# Revit family: 13.3QBR,QBR-M_231217_1
name_source: partatom
category: 통신 장치
units: mm (PartAtom-declared; Revit-internal decimal feet)

## family parameters
OmniClass 번호 = 23.85.10.14.24
OmniClass 제목 = Video Monitors
공유 = 아니오
로드될 때 보이드를 사용하여 절단 = 아니오
룸 계산 점 = 아니오
부품 유형 = 보통
원형 커넥터 치수 = 지름 사용
작업 기준면 기반 = 아니오
주석 방향을 유지합니다. = 아니오
항상 수직 = 예

## types (2) — shared parameters
Active Display Area = 293.76 (H) x 165.24 (V)
Bezel Width (mm) = 12.2  [stored 0.0400262 ft]
Color Gamut = 45%
Contrast Ratio (Typ.) = 800:1
Diagonal Size (Class) = 13
Diagonal Size (Measured) = 13.27
Dimension Package (mm) = 376 x 132 x 248
Dimension Set (mm) = 322.0 x 193.5 x 28.2
Dimension Set Depth (mm) = 28.2
Dimension Set Height (mm) = 193.5  [stored 0.634843 ft]
Dimension Set Width (mm) = 322  [stored 1.05643 ft]
Display Colors = 16.7 M (real 6bit, dither 8bit)
Dynamic C/R = MEGA
EMC = Class B
Environment = ENERGY STAR 8.0, EPEAT
External Control = RS232C(in/out) thru stereo jack, RJ45
H-Scanning Frequency = 30 ~ 81kHZ
Haze = 10%
Input HDCP = HDCP 2.2
Input RGB = -
Input USB = USB 2.0 x 1
Input Video = HDMI 1.4 (1)
Internal Clock Speed = 1.7GHz
Internal Graphics = Graphic resolution : 1920x1080, Output resolution : 1920x1080 (Scale up from graphic processing result.)
Internal IO Ports = USB 2.0
Internal Main Memory Interface = 2.5GB, LPDDR4 1.5GHz 64bit
Internal Multimedia = Video Decoder  : MPEG-1/2/4, H.263, H.264/AVC, UHD H.264/AVC,  VC-1, HEVC, JPEG, PNG, VP8, VP9  *Audio Decoder : AC3 (DD), MPEG
Internal On-Chip Cache Memory = L1 Instruction Cache : 48KB, L1 Data Cache : 32KB, L2 Cache : 2MB
Internal Operating System = Tizen 4.0 (VDLinux)
Internal Processor = Cortex A72 1.7GHz Quad-Core CPU
Internal Storage (FDM) = 8GB (3.88GB Occupied by O/S, 4.12GB Available)
Key = Small Signage Display Slim & Light Signage with Built-in MagicInfo S6, SSSP 6.0
Maximum Pixel Frequency = 594MHz
Operation Hour = 16/7
Optional Mount = -
Optional Specialty = -
Optional Stand = Bar Type Simple Stand(inbox)
Orientation = Landscape / Portrait
Output Audio = Stereo mini Jack
Pixel Pitch (mm) = 0.153 x 0.153
Power Consumption BTU(Max) = 93.8
Power Consumption Max [W/h] = 27.5
Power Consumption Rating [W/h] = 25
Power Consumption Sleep mode = 0.5
Power Consumption Typical [W/h] = 13
Power Supply = AC100 - 240V, 50/60 Hz
Power Type = Adapter
Relative Humidity = 10~80%
Resolution = FHD (1920 x 1080)
Response Time (GtoG) = 8ms
Safety = 60950-1
Screen = Samsung Electronics Screen
Security = 802.1 x (WPA2 Enterprise) : EAP-TLS, EAP-TTLS, EAP-PEAP
Sound = Built in Speaker(5W)
Stand Type = Bar Type Simple Stand (Inbox)
Temperature = 0℃ ~ 40℃
Type = Edge LED
V-Scanning Frequency = 48 ~ 75HZ
VESA Mount = 100 x 100
Viewing Angle(H/V) = 178/178
Weight Set (kg) = 0.9
제조업체 = Samsung Electronics Co., Ltd.
조합 코드 = E1020500
키노트 = 11 52 00

## per-type parameters (varying)
| type | Brightness (Typ.) | Weight Package (kg) |
| Small Signage QB13R | 300 | 1.7(TBD) |
| Small Signage QB13R-M | 500 | 1.7 |

note: column(s) folded — value = type name in every type: 모델

note: [stored X ft] marks values corroborated as IEEE doubles in the binary element streams (Revit-internal decimal feet)
